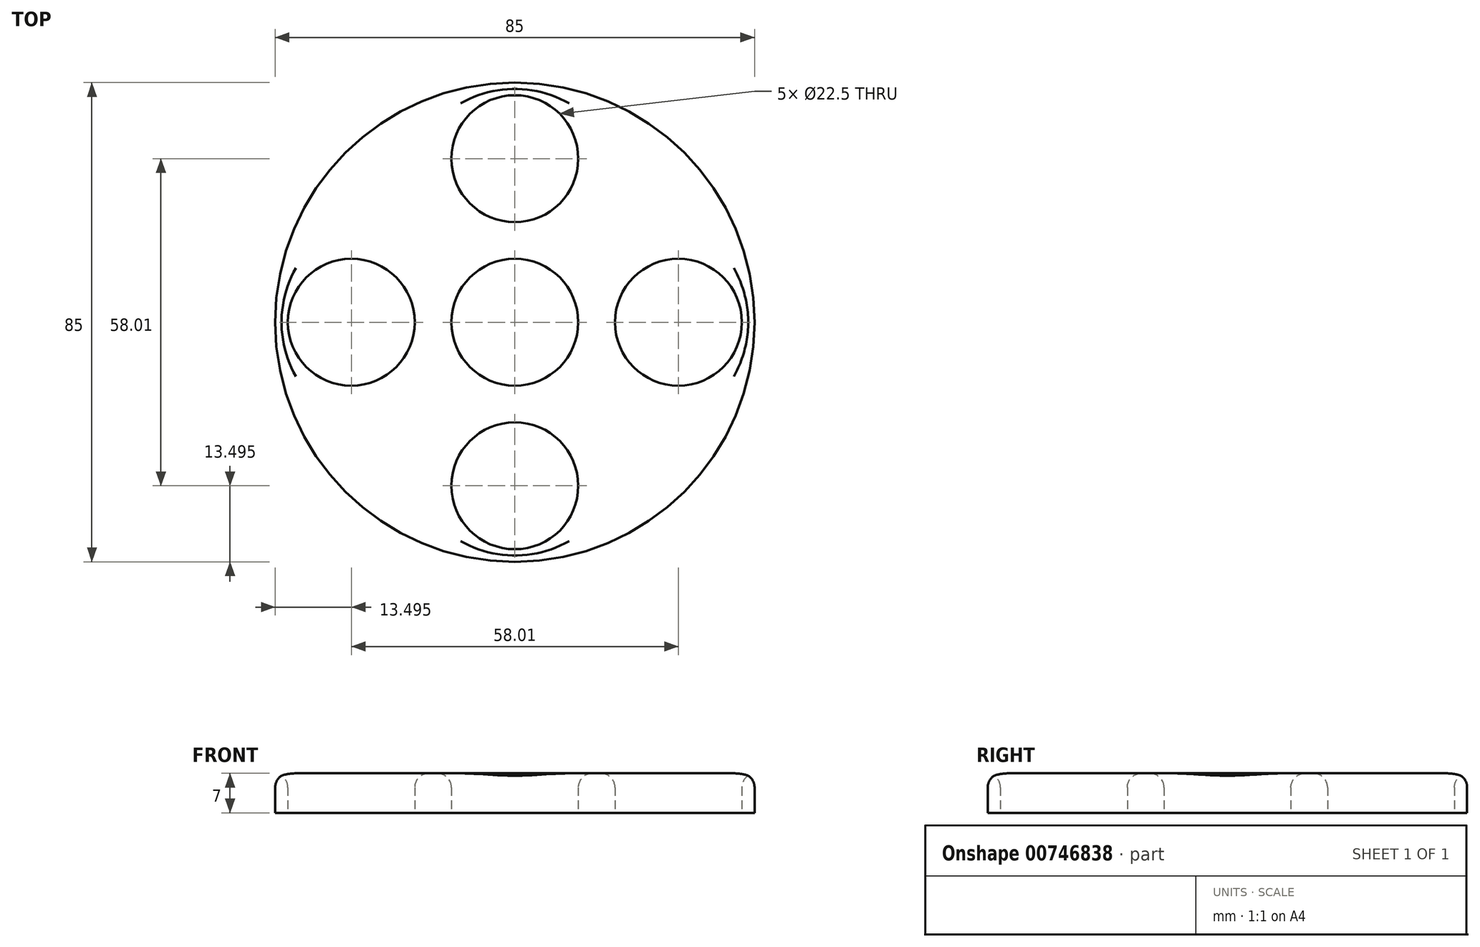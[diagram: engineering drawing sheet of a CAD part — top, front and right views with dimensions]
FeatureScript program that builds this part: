
annotation { "Feature Type Name" : "Feature", "Feature Type Description" : "" }
export const myFeature = defineFeature(function(context is Context, id is Id, definition is map)
    precondition{}
    {
        {
            var Q0;
            Q0=qCreatedBy(makeId("Top.planeOp"),FACE);
            var sketch = newSketch(context, id + "F0", { "sketchPlane" : qUnion([Q0])});
            skCircle(sketch, "E0", {"center": v(0, 0) * mm, "radius": 11.25 * mm});
            skCircle(sketch, "E1", {"center": v(0, 29) * mm, "radius": 11.25 * mm});
            skCircle(sketch, "E2.1.0", {"center": v(-29, 0) * mm, "radius": 11.25 * mm});
            skCircle(sketch, "E2.2.0", {"center": v(0, -29) * mm, "radius": 11.25 * mm});
            skCircle(sketch, "E2.3.0", {"center": v(29, 0) * mm, "radius": 11.25 * mm});
            skCircle(sketch, "E3", {"center": v(0, 0) * mm, "radius": 42.5 * mm});
            skSolve(sketch);
        }
        {
            var Q0;
            Q0=makeQuery(id+"F0.imprint","IMPRINT",FACE,{"disambiguationData":[TD([[makeQuery(id+"F0.imprint","IMPRINT",EDGE,{"derivedFrom":sQuery(id+"F0.wireOp",EDGE,"E0")}),-1.0]])]});
            extrude(context, id + "F1", {"entities" : qUnion([Q0]), "depth" : 7 * mm, "offsetDistance" : 25 * mm});
        }
        {
            var Q0;
            Q0=makeQuery(id+"F1.opExtrude","CAP_FACE",FACE,{"disambiguationData":[OSD([sQuery(id+"F0.wireOp",EDGE,"E0"),sQuery(id+"F0.wireOp",EDGE,"E1"),sQuery(id+"F0.wireOp",EDGE,"E2.1.0"),sQuery(id+"F0.wireOp",EDGE,"E2.2.0"),sQuery(id+"F0.wireOp",EDGE,"E2.3.0"),sQuery(id+"F0.wireOp",EDGE,"E3")])],"isStart":false});
            fillet(context, id + "F2", {"entities" : qUnion([Q0]), "radius" : 2.5 * mm, "tangentPropagation" : true, "allowEdgeOverflow" : false});
        }
    });
